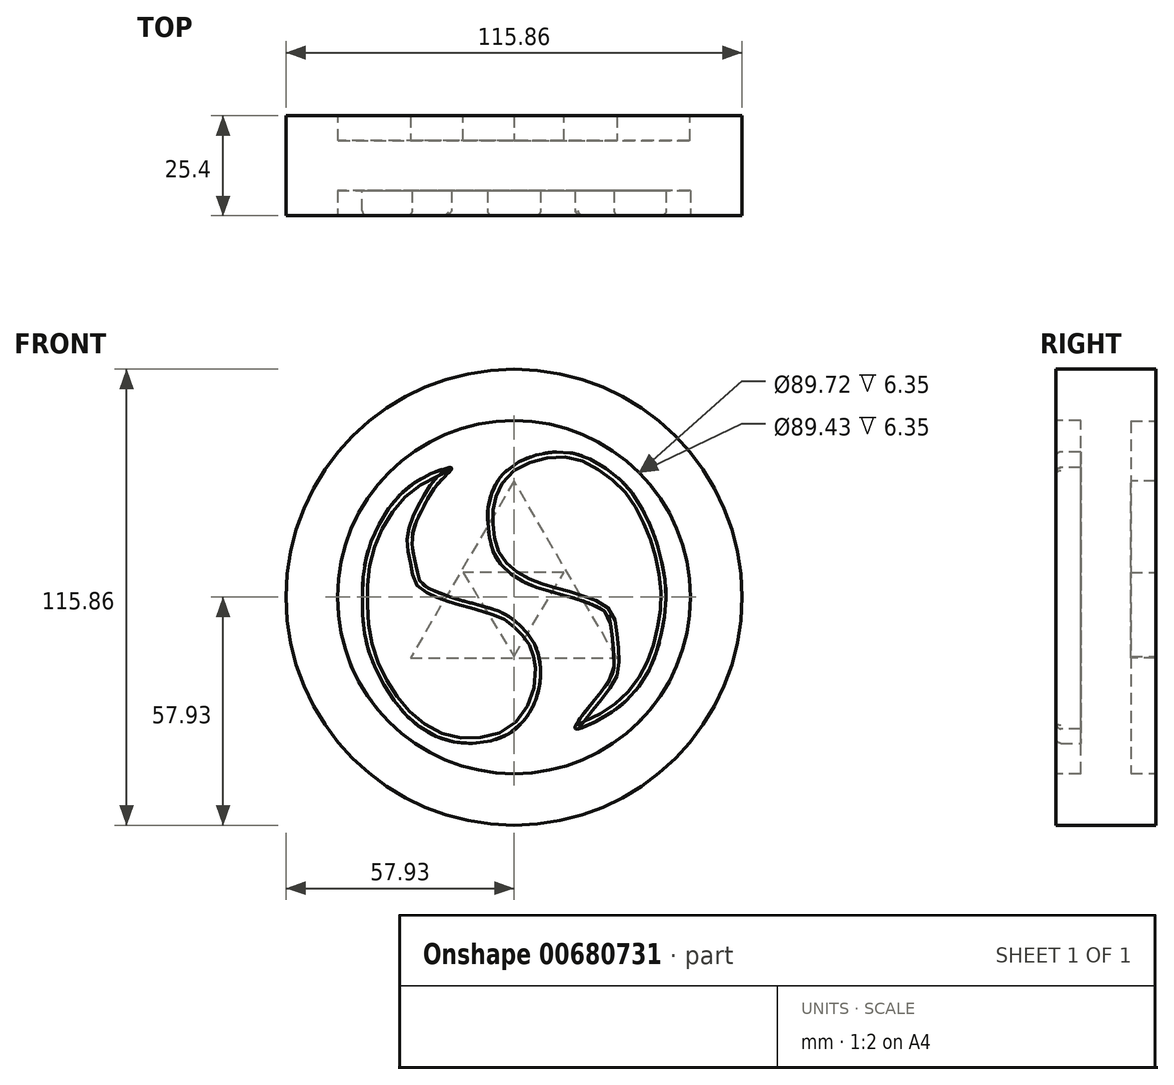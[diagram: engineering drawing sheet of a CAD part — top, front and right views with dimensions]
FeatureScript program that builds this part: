
annotation { "Feature Type Name" : "Feature", "Feature Type Description" : "" }
export const myFeature = defineFeature(function(context is Context, id is Id, definition is map)
    precondition{}
    {
        {
            var Q0;
            Q0=qCreatedBy(makeId("Front.planeOp"),FACE);
            var sketch = newSketch(context, id + "F0", { "sketchPlane" : qUnion([Q0])});
            skCircle(sketch, "E0", {"center": v(0, 0) * mm, "radius": 57.93 * mm});
            skCircle(sketch, "E1", {"center": v(0, 0) * mm, "radius": 45.24 * mm});
            skLineSegment(sketch, "E2", {"start": v(-24.01, 26.9) * mm, "end": v(-4.53, 1.77) * mm});
            skLineSegment(sketch, "E3", {"start": v(-4.53, 1.77) * mm, "end": v(-36.03, 4.88) * mm});
            skLineSegment(sketch, "E4", {"start": v(-36.03, 4.88) * mm, "end": v(-24.01, 26.9) * mm});
            skCircle(sketch, "E5", {"center": v(0, 29.6) * mm, "radius": 10.34 * mm});
            skLineSegment(sketch, "E6", {"start": v(4.46, 1.76) * mm, "end": v(24, 26.88) * mm});
            skLineSegment(sketch, "E7", {"start": v(24, 26.88) * mm, "end": v(36.16, 4.84) * mm});
            skLineSegment(sketch, "E8", {"start": v(36.16, 4.84) * mm, "end": v(4.46, 1.76) * mm});
            skLineSegment(sketch, "E9", {"start": v(0, -5.39) * mm, "end": v(12.64, -34.5) * mm});
            skLineSegment(sketch, "E10", {"start": v(12.64, -34.5) * mm, "end": v(-12.54, -34.5) * mm});
            skLineSegment(sketch, "E11", {"start": v(-12.54, -34.5) * mm, "end": v(0, -5.39) * mm});
            skCircle(sketch, "E12", {"center": v(-26.13, -15.37) * mm, "radius": 10.23 * mm});
            skCircle(sketch, "E13", {"center": v(26.13, -15.19) * mm, "radius": 9.93 * mm});
            skSolve(sketch);
        }
        {
            var Q0;
            Q0=makeQuery(id+"F0.imprint","IMPRINT",FACE,{"disambiguationData":[TD([[makeQuery(id+"F0.imprint","IMPRINT",EDGE,{"derivedFrom":sQuery(id+"F0.wireOp",EDGE,"E0")}),1.0]])]});
            var Q1;
            Q1=makeQuery(id+"F0.imprint","IMPRINT",FACE,{"disambiguationData":[TD([[makeQuery(id+"F0.imprint","IMPRINT",EDGE,{"derivedFrom":sQuery(id+"F0.wireOp",EDGE,"E1")}),1.0]])]});
            var Q2;
            Q2=makeQuery(id+"F0.imprint","IMPRINT",FACE,{"disambiguationData":[TD([[makeQuery(id+"F0.imprint","IMPRINT",EDGE,{"derivedFrom":sQuery(id+"F0.wireOp",EDGE,"E5")}),1.0]])]});
            var Q3;
            Q3=makeQuery(id+"F0.imprint","IMPRINT",FACE,{"disambiguationData":[TD([[makeQuery(id+"F0.imprint","IMPRINT",EDGE,{"derivedFrom":sQuery(id+"F0.wireOp",EDGE,"E2")}),-1.0]])]});
            var Q4;
            Q4=makeQuery(id+"F0.imprint","IMPRINT",FACE,{"disambiguationData":[TD([[makeQuery(id+"F0.imprint","IMPRINT",EDGE,{"derivedFrom":sQuery(id+"F0.wireOp",EDGE,"E12")}),1.0]])]});
            var Q5;
            Q5=makeQuery(id+"F0.imprint","IMPRINT",FACE,{"disambiguationData":[TD([[makeQuery(id+"F0.imprint","IMPRINT",EDGE,{"derivedFrom":sQuery(id+"F0.wireOp",EDGE,"E9")}),-1.0]])]});
            var Q6;
            Q6=makeQuery(id+"F0.imprint","IMPRINT",FACE,{"disambiguationData":[TD([[makeQuery(id+"F0.imprint","IMPRINT",EDGE,{"derivedFrom":sQuery(id+"F0.wireOp",EDGE,"E13")}),1.0]])]});
            var Q7;
            Q7=makeQuery(id+"F0.imprint","IMPRINT",FACE,{"disambiguationData":[TD([[makeQuery(id+"F0.imprint","IMPRINT",EDGE,{"derivedFrom":sQuery(id+"F0.wireOp",EDGE,"E6")}),-1.0]])]});
            extrude(context, id + "F1", {"entities" : qUnion([Q0, Q1, Q2, Q3, Q4, Q5, Q6, Q7]), "depth" : 12.7 * mm, "offsetDistance" : 25.4 * mm});
        }
        {
            var Q0;
            Q0=makeQuery(id+"F1.opExtrude","CAP_FACE",FACE,{"disambiguationData":[OSD([sQuery(id+"F0.wireOp",EDGE,"E0")])],"isStart":true});
            extrude(context, id + "F2", {"entities" : qUnion([Q0]), "operationType" : NewBodyOperationType.ADD, "depth" : 12.7 * mm, "offsetDistance" : 25.4 * mm});
        }
        {
            var Q0;
            Q0=makeQuery(id+"F1.opExtrude","CAP_FACE",FACE,{"disambiguationData":[OSD([sQuery(id+"F0.wireOp",EDGE,"E0")])],"isStart":false});
            var sketch = newSketch(context, id + "F3", { "sketchPlane" : qUnion([Q0])});
            skCircle(sketch, "E14", {"center": v(0, 0) * mm, "radius": 44.86 * mm});
            skSolve(sketch);
        }
        {
            var Q0;
            Q0=makeQuery(id+"F3.imprint","IMPRINT",FACE,{"disambiguationData":[TD([[makeQuery(id+"F3.imprint","IMPRINT",EDGE,{"derivedFrom":sQuery(id+"F3.wireOp",EDGE,"E14")}),1.0]])]});
            extrude(context, id + "F4", {"entities" : qUnion([Q0]), "operationType" : NewBodyOperationType.REMOVE, "oppositeDirection" : true, "depth" : 6.35 * mm, "offsetDistance" : 25.4 * mm});
        }
        {
            var Q0;
            Q0=makeQuery(id+"F2.opExtrude","CAP_FACE",FACE,{"disambiguationData":[OSD([sQuery(id+"F0.wireOp",EDGE,"E0")])],"isStart":false});
            var sketch = newSketch(context, id + "F5", { "sketchPlane" : qUnion([Q0])});
            skCircle(sketch, "E15", {"center": v(0, 0) * mm, "radius": 44.72 * mm});
            skSolve(sketch);
        }
        {
            var Q0;
            Q0=makeQuery(id+"F5.imprint","IMPRINT",FACE,{"disambiguationData":[TD([[makeQuery(id+"F5.imprint","IMPRINT",EDGE,{"derivedFrom":sQuery(id+"F5.wireOp",EDGE,"E15")}),1.0]])]});
            extrude(context, id + "F6", {"entities" : qUnion([Q0]), "operationType" : NewBodyOperationType.REMOVE, "oppositeDirection" : true, "depth" : 6.35 * mm, "offsetDistance" : 25.4 * mm});
        }
        {
            var Q0;
            Q0=makeQuery(id+"F6.boolean.opBoolean","COPY",FACE,{"derivedFrom":makeQuery(id+"F6.opExtrude","CAP_FACE",FACE,{"disambiguationData":[OSD([sQuery(id+"F5.wireOp",EDGE,"E15")])],"isStart":false})});
            var sketch = newSketch(context, id + "F7", { "sketchPlane" : qUnion([Q0])});
            skLineSegment(sketch, "E16", {"start": v(0, 29.52) * mm, "end": v(26.34, -15.44) * mm});
            skLineSegment(sketch, "E17", {"start": v(26.34, -15.44) * mm, "end": v(-26.11, -15.44) * mm});
            skLineSegment(sketch, "E18", {"start": v(-26.11, -15.44) * mm, "end": v(0, 29.52) * mm});
            skLineSegment(sketch, "E19", {"start": v(13.17, 7.04) * mm, "end": v(0.11, -15.44) * mm});
            skLineSegment(sketch, "E20", {"start": v(0.11, -15.44) * mm, "end": v(-13.06, 7.04) * mm});
            skLineSegment(sketch, "E21", {"start": v(-13.06, 7.04) * mm, "end": v(13.17, 7.04) * mm});
            skSolve(sketch);
        }
        {
            var Q0;
            {var subQ3=sQuery(id+"F7.wireOp",EDGE,"E20");Q0=makeQuery(id+"F7.imprint","IMPRINT",FACE,{"disambiguationData":[TD([[makeQuery(id+"F7.imprint","IMPRINT",EDGE,{"derivedFrom":subQ3}),1.0]])]});}
            var Q1;
            Q1=makeQuery(id+"F7.imprint","IMPRINT",FACE,{"disambiguationData":[TD([[makeQuery(id+"F7.imprint","IMPRINT",EDGE,{"derivedFrom":sQuery(id+"F7.wireOp",EDGE,"E19")}),-1.0]])]});
            var Q2;
            {var subQ3=sQuery(id+"F7.wireOp",EDGE,"E21");Q2=makeQuery(id+"F7.imprint","IMPRINT",FACE,{"disambiguationData":[TD([[makeQuery(id+"F7.imprint","IMPRINT",EDGE,{"derivedFrom":subQ3}),1.0]])]});}
            var Q3;
            {var subQ3=sQuery(id+"F7.wireOp",EDGE,"E19");Q3=makeQuery(id+"F7.imprint","IMPRINT",FACE,{"disambiguationData":[TD([[makeQuery(id+"F7.imprint","IMPRINT",EDGE,{"derivedFrom":subQ3}),1.0]])]});}
            extrude(context, id + "F8", {"entities" : qUnion([Q0, Q1, Q2, Q3]), "operationType" : NewBodyOperationType.ADD, "depth" : 6.35 * mm, "offsetDistance" : 25.4 * mm});
        }
        {
            var Q0;
            Q0=makeQuery(id+"F8.opExtrude","CAP_FACE",FACE,{"disambiguationData":[OSD([sQuery(id+"F7.wireOp",EDGE,"E16"),sQuery(id+"F7.wireOp",EDGE,"E17"),sQuery(id+"F7.wireOp",EDGE,"E18")])],"isStart":false});
            var sketch = newSketch(context, id + "F9", { "sketchPlane" : qUnion([Q0])});
            skLineSegment(sketch, "E22", {"start": v(-12.72, 6.35) * mm, "end": v(12.98, 6.35) * mm});
            skLineSegment(sketch, "E23", {"start": v(12.98, 6.35) * mm, "end": v(0, -15) * mm});
            skLineSegment(sketch, "E24", {"start": v(0, -15) * mm, "end": v(-12.72, 6.35) * mm});
            skSolve(sketch);
        }
        {
            var Q0;
            Q0=makeQuery(id+"F9.imprint","IMPRINT",FACE,{"disambiguationData":[TD([[makeQuery(id+"F9.imprint","IMPRINT",EDGE,{"derivedFrom":sQuery(id+"F9.wireOp",EDGE,"E22")}),-1.0]])]});
            extrude(context, id + "F10", {"entities" : qUnion([Q0]), "operationType" : NewBodyOperationType.REMOVE, "oppositeDirection" : true, "depth" : 6.35 * mm, "offsetDistance" : 25.4 * mm});
        }
        {
            var Q0;
            Q0=makeQuery(id+"F4.boolean.opBoolean","COPY",FACE,{"derivedFrom":makeQuery(id+"F4.opExtrude","CAP_FACE",FACE,{"disambiguationData":[OSD([sQuery(id+"F3.wireOp",EDGE,"E14")])],"isStart":false})});
            var sketch = newSketch(context, id + "F11", { "sketchPlane" : qUnion([Q0])});
            skFitSpline(sketch, "E25", {"points": [v(-2.57, 31.55) * mm, v(4.74, 35.84) * mm, v(11.83, 36.9) * mm, v(18.08, 35.63) * mm, v(24.83, 31.62) * mm, v(29.74, 26.85) * mm, v(33.89, 19.9) * mm, v(36.84, 11.75) * mm, v(38.52, 2.83) * mm, v(38.3, -4.27) * mm, v(36.37, -13.34) * mm, v(32.6, -21.41) * mm, v(26.72, -27.9) * mm, v(18.95, -32.48) * mm, v(15.49, -33.26) * mm, v(23.37, -22.42) * mm, v(25.43, -16.38) * mm, v(24.6, -7.44) * mm, v(23.26, -3.8) * mm, v(14.37, 0) * mm, v(3.3, 3.46) * mm, v(-2.5, 7.49) * mm, v(-5.32, 11.74) * mm, v(-6.6, 18.25) * mm, v(-6.32, 24.3) * mm, v(-2.57, 31.55) * mm]});
            skFitSpline(sketch, "E26", {"points": [v(2.2, -31.72) * mm, v(6.2, -23.75) * mm, v(5.63, -12.9) * mm, v(1.01, -6.74) * mm, v(-3.33, -3.8) * mm, v(-12.14, -1.15) * mm, v(-18.3, 0.81) * mm, v(-22.08, 2.5) * mm, v(-23.86, 3.99) * mm, v(-24.71, 7.24) * mm, v(-25.81, 12.73) * mm, v(-25.38, 17.74) * mm, v(-22.72, 23.49) * mm, v(-19.11, 29.12) * mm, v(-15.87, 32.82) * mm, v(-23.97, 29.9) * mm, v(-32.53, 21.49) * mm, v(-37.31, 11.08) * mm, v(-38.54, 0) * mm, v(-37.62, -10.98) * mm, v(-33.92, -20.7) * mm, v(-28.19, -29.13) * mm, v(-21.93, -34.27) * mm, v(-15.35, -36.74) * mm, v(-8.39, -36.94) * mm, v(-2.33, -35.24) * mm, v(2.2, -31.72) * mm]});
            skSolve(sketch);
        }
        {
            var Q0;
            Q0=makeQuery(id+"F11.imprint","IMPRINT",FACE,{"disambiguationData":[TD([[makeQuery(id+"F11.imprint","IMPRINT",EDGE,{"derivedFrom":sQuery(id+"F11.wireOp",EDGE,"E26")}),1.0]])]});
            var Q1;
            Q1=makeQuery(id+"F11.imprint","IMPRINT",FACE,{"disambiguationData":[TD([[makeQuery(id+"F11.imprint","IMPRINT",EDGE,{"derivedFrom":sQuery(id+"F11.wireOp",EDGE,"E25")}),-1.0]])]});
            extrude(context, id + "F12", {"entities" : qUnion([Q0, Q1]), "operationType" : NewBodyOperationType.ADD, "depth" : 6.35 * mm, "offsetDistance" : 25.4 * mm});
        }
        {
            var Q0;
            Q0=makeQuery(id+"F12.opExtrude","CAP_FACE",FACE,{"disambiguationData":[OSD([sQuery(id+"F11.wireOp",EDGE,"E26")])],"isStart":false});
            fillet(context, id + "F13", {"entities" : qUnion([Q0]), "radius" : 1.27 * mm, "tangentPropagation" : true, "allowEdgeOverflow" : false});
        }
        {
            var Q0;
            Q0=makeQuery(id+"F12.opExtrude","CAP_FACE",FACE,{"disambiguationData":[OSD([sQuery(id+"F11.wireOp",EDGE,"E25")])],"isStart":false});
            fillet(context, id + "F14", {"entities" : qUnion([Q0]), "radius" : 1.27 * mm, "tangentPropagation" : true, "allowEdgeOverflow" : false});
        }
    });
